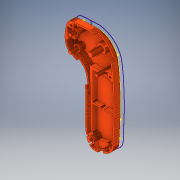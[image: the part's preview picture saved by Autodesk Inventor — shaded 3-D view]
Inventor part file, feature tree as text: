
AUTODESK INVENTOR PART (.ipt)
format: ipt  version: 2019.4 (Build 234330000, 330)  size: 12,588,032 bytes
history: native  units: mm
features: sketch x3, other x2, shell x1, surface_op x1, projected_geometry x1
ambient origin geometry x8: Origin, YZ Plane, XZ Plane, XY Plane, X Axis, Y Axis, Z Axis, Center Point
bodies: Solid1 (feature_tree)
feature tree (8):
  shell  "shell-bottom"  Thickness=5.0mm
  surface_op  "Sculpt1"
  sketch  "Sketch1"
  sketch  "Sketch2"
  sketch  "Sketch3"
  projected_geometry  "Projected Loop1"
  other  "MeshFeature1"
  other  "Srf1"
